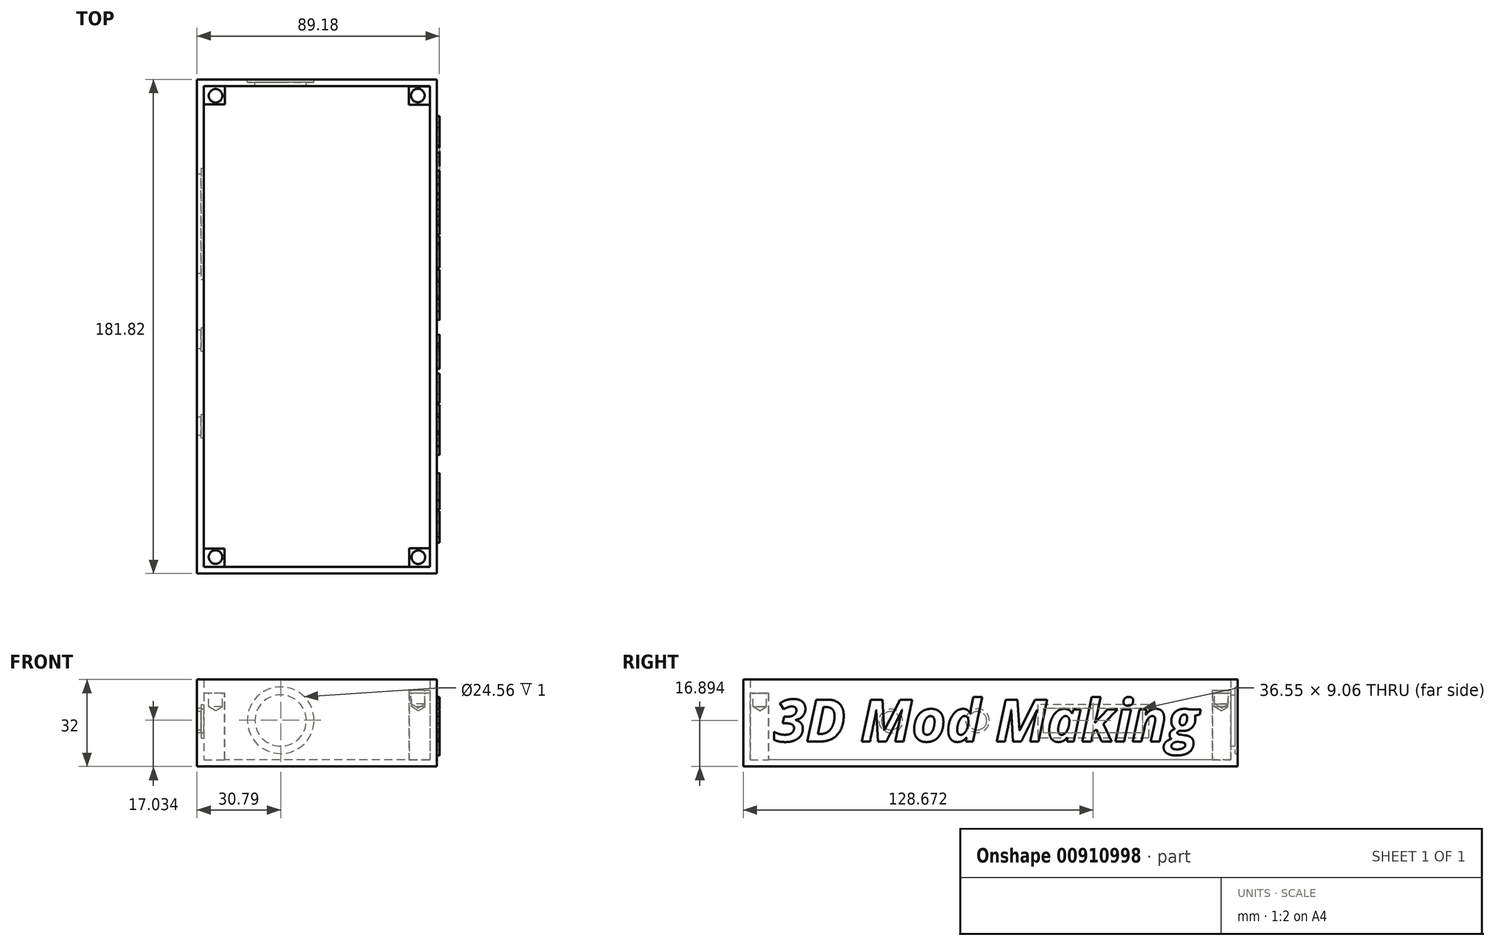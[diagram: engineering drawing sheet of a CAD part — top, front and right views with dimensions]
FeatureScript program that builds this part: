
annotation { "Feature Type Name" : "Feature", "Feature Type Description" : "" }
export const myFeature = defineFeature(function(context is Context, id is Id, definition is map)
    precondition{}
    {
        {
            var Q0;
            Q0=qCreatedBy(makeId("Top.planeOp"),FACE);
            var sketch = newSketch(context, id + "F0", { "sketchPlane" : qUnion([Q0])});
            skLineSegment(sketch, "E0.bottom", {"start": v(44.1, 90.91) * mm, "end": v(-44.1, 90.91) * mm});
            skLineSegment(sketch, "E0.top", {"start": v(44.1, -90.91) * mm, "end": v(-44.1, -90.91) * mm});
            skLineSegment(sketch, "E0.left", {"start": v(44.1, 90.91) * mm, "end": v(44.1, -90.91) * mm});
            skLineSegment(sketch, "E0.right", {"start": v(-44.1, 90.91) * mm, "end": v(-44.1, -90.91) * mm});
            skPoint(sketch, "E0.middle", {"position": v(0, 0) * mm});
            skSolve(sketch);
        }
        {
            var Q0;
            Q0=qSketchRegion(id+"F0",true);
            extrude(context, id + "F1", {"entities" : qUnion([Q0]), "depth" : 32 * mm, "offsetDistance" : 25 * mm});
        }
        {
            var Q0;
            Q0=makeQuery(id+"F1.opExtrude","CAP_FACE",FACE,{"disambiguationData":[OSD([sQuery(id+"F0.wireOp",EDGE,"E0.bottom"),sQuery(id+"F0.wireOp",EDGE,"E0.top"),sQuery(id+"F0.wireOp",EDGE,"E0.left"),sQuery(id+"F0.wireOp",EDGE,"E0.right")])],"isStart":false});
            shell(context, id + "F2", {"entities" : qUnion([Q0]), "thickness" : 2.5 * mm});
        }
        {
            var Q0;
            Q0=qCreatedBy(makeId("Top.planeOp"),FACE);
            var sketch = newSketch(context, id + "F3", { "sketchPlane" : qUnion([Q0])});
            skLineSegment(sketch, "E1.bottom", {"start": v(41.57, 88.4) * mm, "end": v(33.87, 88.4) * mm});
            skLineSegment(sketch, "E1.top", {"start": v(41.57, 81.63) * mm, "end": v(33.87, 81.63) * mm});
            skLineSegment(sketch, "E1.left", {"start": v(41.57, 88.4) * mm, "end": v(41.57, 81.63) * mm});
            skLineSegment(sketch, "E1.right", {"start": v(33.87, 88.4) * mm, "end": v(33.87, 81.63) * mm});
            skSolve(sketch);
        }
        {
            var Q0;
            Q0=qSketchRegion(id+"F3",true);
            extrude(context, id + "F4", {"entities" : qUnion([Q0]), "operationType" : NewBodyOperationType.ADD, "depth" : 28 * mm, "offsetDistance" : 25 * mm});
        }
        {
            var Q0;
            Q0=qCreatedBy(makeId("Top.planeOp"),FACE);
            var sketch = newSketch(context, id + "F5", { "sketchPlane" : qUnion([Q0])});
            skLineSegment(sketch, "E2.bottom", {"start": v(-33.9, 88.46) * mm, "end": v(-41.6, 88.46) * mm});
            skLineSegment(sketch, "E2.top", {"start": v(-33.9, 81.7) * mm, "end": v(-41.6, 81.7) * mm});
            skLineSegment(sketch, "E2.left", {"start": v(-33.9, 88.46) * mm, "end": v(-33.9, 81.7) * mm});
            skLineSegment(sketch, "E2.right", {"start": v(-41.6, 88.46) * mm, "end": v(-41.6, 81.7) * mm});
            skSolve(sketch);
        }
        {
            var Q0;
            Q0=qSketchRegion(id+"F5",true);
            extrude(context, id + "F6", {"entities" : qUnion([Q0]), "operationType" : NewBodyOperationType.ADD, "depth" : 27 * mm, "offsetDistance" : 25 * mm});
        }
        {
            var Q0;
            Q0=qCreatedBy(makeId("Top.planeOp"),FACE);
            var sketch = newSketch(context, id + "F7", { "sketchPlane" : qUnion([Q0])});
            skLineSegment(sketch, "E3.bottom", {"start": v(-33.97, -81.7) * mm, "end": v(-41.67, -81.7) * mm});
            skLineSegment(sketch, "E3.top", {"start": v(-33.97, -88.47) * mm, "end": v(-41.67, -88.47) * mm});
            skLineSegment(sketch, "E3.left", {"start": v(-33.97, -81.7) * mm, "end": v(-33.97, -88.47) * mm});
            skLineSegment(sketch, "E3.right", {"start": v(-41.67, -81.7) * mm, "end": v(-41.67, -88.47) * mm});
            skSolve(sketch);
        }
        {
            var Q0;
            Q0=qSketchRegion(id+"F7",true);
            extrude(context, id + "F8", {"entities" : qUnion([Q0]), "operationType" : NewBodyOperationType.ADD, "depth" : 27 * mm, "offsetDistance" : 25 * mm});
        }
        {
            var Q0;
            Q0=qCreatedBy(makeId("Top.planeOp"),FACE);
            var sketch = newSketch(context, id + "F9", { "sketchPlane" : qUnion([Q0])});
            skLineSegment(sketch, "E4.bottom", {"start": v(41.62, -81.63) * mm, "end": v(33.92, -81.63) * mm});
            skLineSegment(sketch, "E4.top", {"start": v(41.62, -88.4) * mm, "end": v(33.92, -88.4) * mm});
            skLineSegment(sketch, "E4.left", {"start": v(41.62, -81.63) * mm, "end": v(41.62, -88.4) * mm});
            skLineSegment(sketch, "E4.right", {"start": v(33.92, -81.63) * mm, "end": v(33.92, -88.4) * mm});
            skSolve(sketch);
        }
        {
            var Q0;
            Q0=qSketchRegion(id+"F9",true);
            extrude(context, id + "F10", {"entities" : qUnion([Q0]), "operationType" : NewBodyOperationType.ADD, "depth" : 27 * mm, "offsetDistance" : 25 * mm});
        }
        {
            var Q0;
            Q0=makeQuery(id+"F4.opExtrude","CAP_FACE",FACE,{"disambiguationData":[OSD([sQuery(id+"F3.wireOp",EDGE,"E1.bottom"),sQuery(id+"F3.wireOp",EDGE,"E1.top"),sQuery(id+"F3.wireOp",EDGE,"E1.left"),sQuery(id+"F3.wireOp",EDGE,"E1.right")])],"isStart":false});
            var sketch = newSketch(context, id + "F11", { "sketchPlane" : qUnion([Q0])});
            skCircle(sketch, "E5", {"center": v(37.15, 85) * mm, "radius": 2.37 * mm});
            skSolve(sketch);
        }
        {
            var Q0;
            Q0=sQuery(id+"F11.wireOp",VERTEX,"E5.center");
            var Q1;
            Q1=makeQuery(id+"F1.opExtrude","SWEPT_BODY",BODY,{"disambiguationData":[OSD([sQuery(id+"F0.wireOp",EDGE,"E0.bottom"),sQuery(id+"F0.wireOp",EDGE,"E0.top"),sQuery(id+"F0.wireOp",EDGE,"E0.left"),sQuery(id+"F0.wireOp",EDGE,"E0.right")])]});
            hole(context, id + "F12", {"style" : HoleStyle.SIMPLE, "endStyle" : HoleEndStyle.BLIND, "holeDiameter" : 5 * mm, "majorDiameter" : 5 * mm, "holeDepth" : 5 * mm, "isTappedThrough" : true, "tappedDepth" : 12 * mm, "tapClearance" : 3, "locations" : qUnion([Q0]), "scope" : qUnion([Q1])});
        }
        {
            var Q0;
            Q0=makeQuery(id+"F10.opExtrude","CAP_FACE",FACE,{"disambiguationData":[OSD([sQuery(id+"F9.wireOp",EDGE,"E4.bottom"),sQuery(id+"F9.wireOp",EDGE,"E4.top"),sQuery(id+"F9.wireOp",EDGE,"E4.left"),sQuery(id+"F9.wireOp",EDGE,"E4.right")])],"isStart":false});
            var sketch = newSketch(context, id + "F13", { "sketchPlane" : qUnion([Q0])});
            skCircle(sketch, "E6", {"center": v(37.33, -84.9) * mm, "radius": 2.37 * mm});
            skSolve(sketch);
        }
        {
            var Q0;
            Q0=sQuery(id+"F13.wireOp",VERTEX,"E6.center");
            var Q1;
            Q1=makeQuery(id+"F1.opExtrude","SWEPT_BODY",BODY,{"disambiguationData":[OSD([sQuery(id+"F0.wireOp",EDGE,"E0.bottom"),sQuery(id+"F0.wireOp",EDGE,"E0.top"),sQuery(id+"F0.wireOp",EDGE,"E0.left"),sQuery(id+"F0.wireOp",EDGE,"E0.right")])]});
            hole(context, id + "F14", {"style" : HoleStyle.SIMPLE, "endStyle" : HoleEndStyle.BLIND, "holeDiameter" : 5 * mm, "majorDiameter" : 5 * mm, "holeDepth" : 5 * mm, "isTappedThrough" : true, "tappedDepth" : 12 * mm, "tapClearance" : 3, "locations" : qUnion([Q0]), "scope" : qUnion([Q1])});
        }
        {
            var Q0;
            Q0=makeQuery(id+"F8.opExtrude","CAP_FACE",FACE,{"disambiguationData":[OSD([sQuery(id+"F7.wireOp",EDGE,"E3.bottom"),sQuery(id+"F7.wireOp",EDGE,"E3.top"),sQuery(id+"F7.wireOp",EDGE,"E3.left"),sQuery(id+"F7.wireOp",EDGE,"E3.right")])],"isStart":false});
            var sketch = newSketch(context, id + "F15", { "sketchPlane" : qUnion([Q0])});
            skCircle(sketch, "E7", {"center": v(-37.29, -84.82) * mm, "radius": 2.37 * mm});
            skSolve(sketch);
        }
        {
            var Q0;
            Q0=sQuery(id+"F15.wireOp",VERTEX,"E7.center");
            var Q1;
            Q1=makeQuery(id+"F1.opExtrude","SWEPT_BODY",BODY,{"disambiguationData":[OSD([sQuery(id+"F0.wireOp",EDGE,"E0.bottom"),sQuery(id+"F0.wireOp",EDGE,"E0.top"),sQuery(id+"F0.wireOp",EDGE,"E0.left"),sQuery(id+"F0.wireOp",EDGE,"E0.right")])]});
            hole(context, id + "F16", {"style" : HoleStyle.SIMPLE, "endStyle" : HoleEndStyle.BLIND, "holeDiameter" : 5 * mm, "majorDiameter" : 5 * mm, "holeDepth" : 5 * mm, "isTappedThrough" : true, "tappedDepth" : 12 * mm, "tapClearance" : 3, "locations" : qUnion([Q0]), "scope" : qUnion([Q1])});
        }
        {
            var Q0;
            Q0=makeQuery(id+"F6.opExtrude","CAP_FACE",FACE,{"disambiguationData":[OSD([sQuery(id+"F5.wireOp",EDGE,"E2.bottom"),sQuery(id+"F5.wireOp",EDGE,"E2.top"),sQuery(id+"F5.wireOp",EDGE,"E2.left"),sQuery(id+"F5.wireOp",EDGE,"E2.right")])],"isStart":false});
            var sketch = newSketch(context, id + "F17", { "sketchPlane" : qUnion([Q0])});
            skCircle(sketch, "E8", {"center": v(-37.26, 84.89) * mm, "radius": 2.37 * mm});
            skSolve(sketch);
        }
        {
            var Q0;
            Q0=sQuery(id+"F17.wireOp",VERTEX,"E8.center");
            var Q1;
            Q1=makeQuery(id+"F1.opExtrude","SWEPT_BODY",BODY,{"disambiguationData":[OSD([sQuery(id+"F0.wireOp",EDGE,"E0.bottom"),sQuery(id+"F0.wireOp",EDGE,"E0.top"),sQuery(id+"F0.wireOp",EDGE,"E0.left"),sQuery(id+"F0.wireOp",EDGE,"E0.right")])]});
            hole(context, id + "F18", {"style" : HoleStyle.SIMPLE, "endStyle" : HoleEndStyle.BLIND, "holeDiameter" : 5 * mm, "majorDiameter" : 5 * mm, "holeDepth" : 5 * mm, "isTappedThrough" : true, "tappedDepth" : 12 * mm, "tapClearance" : 3, "locations" : qUnion([Q0]), "scope" : qUnion([Q1])});
        }
        {
            var Q0;
            Q0=makeQuery(id+"F2.opShell","OFFSET_FACE",FACE,{"disambiguationData":[OSD([sQuery(id+"F0.wireOp",EDGE,"E0.right")])]});
            var sketch = newSketch(context, id + "F19", { "sketchPlane" : qUnion([Q0])});
            skLineSegment(sketch, "E9.bottom", {"start": v(58.22, 22.8) * mm, "end": v(17.38, 22.8) * mm});
            skLineSegment(sketch, "E9.top", {"start": v(58.22, 10.52) * mm, "end": v(17.38, 10.52) * mm});
            skLineSegment(sketch, "E9.left", {"start": v(58.22, 22.8) * mm, "end": v(58.22, 10.52) * mm});
            skLineSegment(sketch, "E9.right", {"start": v(17.38, 22.8) * mm, "end": v(17.38, 10.52) * mm});
            skSolve(sketch);
        }
        {
            var Q0;
            Q0=makeQuery(id+"F19.imprint","IMPRINT",FACE,{"disambiguationData":[TD([[makeQuery(id+"F19.imprint","IMPRINT",EDGE,{"derivedFrom":sQuery(id+"F19.wireOp",EDGE,"E9.bottom")}),1.0]])]});
            extrude(context, id + "F20", {"entities" : qUnion([Q0]), "operationType" : NewBodyOperationType.REMOVE, "oppositeDirection" : true, "depth" : 1 * mm, "offsetDistance" : 25 * mm});
        }
        {
            var Q0;
            Q0=makeQuery(id+"F1.opExtrude","SWEPT_FACE",FACE,{"disambiguationData":[OSD([sQuery(id+"F0.wireOp",EDGE,"E0.right")])]});
            var sketch = newSketch(context, id + "F21", { "sketchPlane" : qUnion([Q0])});
            skLineSegment(sketch, "E10.bottom", {"start": v(-56.04, 12.36) * mm, "end": v(-19.49, 12.36) * mm});
            skLineSegment(sketch, "E10.top", {"start": v(-56.04, 21.42) * mm, "end": v(-19.49, 21.42) * mm});
            skLineSegment(sketch, "E10.left", {"start": v(-56.04, 12.36) * mm, "end": v(-56.04, 21.42) * mm});
            skLineSegment(sketch, "E10.right", {"start": v(-19.49, 12.36) * mm, "end": v(-19.49, 21.42) * mm});
            skSolve(sketch);
        }
        {
            var Q0;
            Q0=qSketchRegion(id+"F21",true);
            extrude(context, id + "F22", {"entities" : qUnion([Q0]), "operationType" : NewBodyOperationType.REMOVE, "oppositeDirection" : true, "depth" : 2.5 * mm, "offsetDistance" : 25 * mm});
        }
        {
            var Q0;
            Q0=makeQuery(id+"F2.opShell","OFFSET_FACE",FACE,{"disambiguationData":[OSD([sQuery(id+"F0.wireOp",EDGE,"E0.right")])]});
            var sketch = newSketch(context, id + "F23", { "sketchPlane" : qUnion([Q0])});
            skCircle(sketch, "E11", {"center": v(-4.75, 16.86) * mm, "radius": 4.35 * mm});
            skSolve(sketch);
        }
        {
            var Q0;
            Q0=makeQuery(id+"F23.imprint","IMPRINT",FACE,{"disambiguationData":[TD([[makeQuery(id+"F23.imprint","IMPRINT",EDGE,{"derivedFrom":sQuery(id+"F23.wireOp",EDGE,"E11")}),1.0]])]});
            var sketch = newSketch(context, id + "F24", { "sketchPlane" : qUnion([Q0])});
            skCircle(sketch, "E12", {"center": v(-36.65, 16.75) * mm, "radius": 4.35 * mm});
            skSolve(sketch);
        }
        {
            var Q0;
            Q0=qSketchRegion(id+"F24",true);
            var Q1;
            Q1=qSketchRegion(id+"F23",true);
            extrude(context, id + "F25", {"entities" : qUnion([Q0, Q1]), "operationType" : NewBodyOperationType.REMOVE, "oppositeDirection" : true, "depth" : 1 * mm, "offsetDistance" : 25 * mm});
        }
        {
            var Q0;
            Q0=makeQuery(id+"F1.opExtrude","SWEPT_FACE",FACE,{"disambiguationData":[OSD([sQuery(id+"F0.wireOp",EDGE,"E0.right")])]});
            var sketch = newSketch(context, id + "F26", { "sketchPlane" : qUnion([Q0])});
            skCircle(sketch, "E13", {"center": v(36.68, 16.84) * mm, "radius": 3.4 * mm});
            skCircle(sketch, "E14", {"center": v(4.77, 16.84) * mm, "radius": 3.4 * mm});
            skSolve(sketch);
        }
        {
            var Q0;
            Q0=qSketchRegion(id+"F26",true);
            extrude(context, id + "F27", {"entities" : qUnion([Q0]), "operationType" : NewBodyOperationType.REMOVE, "oppositeDirection" : true, "depth" : 2.5 * mm, "offsetDistance" : 25 * mm});
        }
        {
            var Q0;
            Q0=makeQuery(id+"F1.opExtrude","SWEPT_FACE",FACE,{"disambiguationData":[OSD([sQuery(id+"F0.wireOp",EDGE,"E0.bottom")])]});
            var sketch = newSketch(context, id + "F28", { "sketchPlane" : qUnion([Q0])});
            skCircle(sketch, "E15", {"center": v(13.3, 17.03) * mm, "radius": 12.28 * mm});
            skSolve(sketch);
        }
        {
            var Q0;
            Q0=makeQuery(id+"F28.imprint","IMPRINT",FACE,{"disambiguationData":[TD([[makeQuery(id+"F28.imprint","IMPRINT",EDGE,{"derivedFrom":sQuery(id+"F28.wireOp",EDGE,"E15")}),1.0]])]});
            extrude(context, id + "F29", {"entities" : qUnion([Q0]), "operationType" : NewBodyOperationType.REMOVE, "oppositeDirection" : true, "depth" : 1 * mm, "offsetDistance" : 25 * mm});
        }
        {
            var Q0;
            Q0=qSketchRegion(id+"F28",true);
            var sketch = newSketch(context, id + "F30", { "sketchPlane" : qUnion([Q0])});
            skCircle(sketch, "E16", {"center": v(13.32, 16.92) * mm, "radius": 9.44 * mm});
            skSolve(sketch);
        }
        {
            var Q0;
            Q0=qSketchRegion(id+"F30",true);
            extrude(context, id + "F31", {"entities" : qUnion([Q0]), "operationType" : NewBodyOperationType.REMOVE, "oppositeDirection" : true, "depth" : 2.5 * mm, "offsetDistance" : 25 * mm});
        }
        {
            var Q0;
            Q0=makeQuery(id+"F1.opExtrude","SWEPT_FACE",FACE,{"disambiguationData":[OSD([sQuery(id+"F0.wireOp",EDGE,"E0.left")])]});
            var sketch = newSketch(context, id + "F32", { "sketchPlane" : qUnion([Q0])});
            skText(sketch, "E17", { "text": "3D Mod Making", "fontName": "OpenSans-BoldItalic.ttf"});
            const initialGuessF32  = {"E17": [-0.07967, 0.00926, 1, 0, 0.01543]};
            skSetInitialGuess(sketch, initialGuessF32);
            skSolve(sketch);
        }
        {
            var Q0;
            Q0=qSketchRegion(id+"F32",true);
            var Q1;
            Q1=qBodyType(qCreatedBy(id+"F32",EDGE),BodyType.WIRE);
            extrude(context, id + "F33", {"entities" : qUnion([Q0]), "operationType" : NewBodyOperationType.ADD, "surfaceEntities" : qUnion([Q1]), "depth" : 1 * mm, "offsetDistance" : 25 * mm, "hasDraft" : true, "draftAngle" : 3 * degree});
        }
    });
